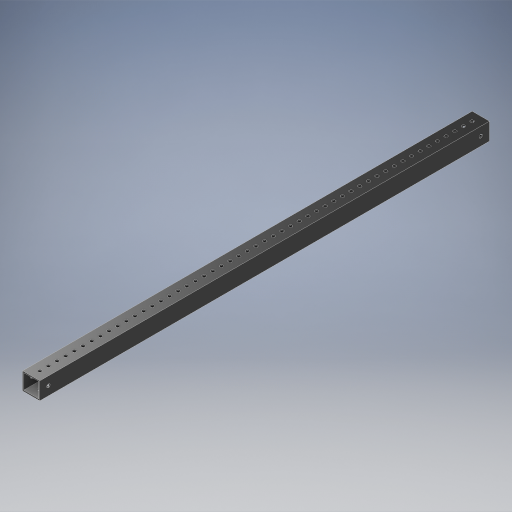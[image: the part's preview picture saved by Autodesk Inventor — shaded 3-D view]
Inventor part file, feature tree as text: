
AUTODESK INVENTOR PART (.ipt)
format: ipt  version: 2024.2 (Build 282272000, 272)  size: 853,504 bytes
history: native  units: in
note: dims shown in document units (in); Inventor stores cm internally (conversion verified against a paired STEP export)
features: other x13, extrude x9, hole x3, pattern_linear x3, mirror x3, sheet_metal_op x1, plane x1
ambient origin geometry x8: Origin, YZ Plane, XZ Plane, XY Plane, X Axis, Y Axis, Z Axis, Center Point
bodies: Solid1 (feature_tree)
feature tree (33):
  other  "Blocks"
  other  "Base Sketch"
  extrude  "Base"  Depth=1.0in
  extrude  "MAX Corner"  Depth=1.0in
  extrude  "MAX Corner Cut"  Depth=0.0625in
  extrude  "Scribe Lines"  Depth=0.0625in
  other  "Side Middle"
  other  "Top Middle"
  other  "Side Holes Sketch"
  hole  "Top Side Hole"  [1 undecoded]
  hole  "Mid Side Hole"  [1 undecoded]
  hole  "Btm Side Hole"  [1 undecoded]
  pattern_linear  "Side Holes"  Spacing1=0.04in  [1 undecoded]
  mirror  "Side Mirror"
  extrude  "MAXTube Hole"  Depth=0.04in
  extrude  "MAXTube Outside"  Depth=26.0in
  pattern_linear  "MAXTube Pattern"  Spacing1=0.0in  [1 undecoded]
  mirror  "MAXTube Mirror"
  extrude  "Left Top Hole"  Depth=26.0in
  extrude  "Mid Top Hole"  TaperAngle=0.0deg  [1 undecoded]
  extrude  "Right Top Hole"  TaperAngle=0.0deg  [1 undecoded]
  pattern_linear  "Top Holes"  Spacing1=0.005in  [1 undecoded]
  mirror  "Top Mirror"
  sheet_metal_op  "Corner"
  other  "MAXTube"
  plane  "Work Plane3"
  other  "Corner:5"
  other  "Corner:6"
  other  "Corner:7"
  other  "Corner:8"
  other  "MAXTube:1"
  other  "MAXTube:2"
  other  "MAXTube:3"
note: 8 required parameter values undecoded (feature->parameter linkage not recoverable at this tier; creation-order binding heuristic only, values carry confidence <= 0.55)
